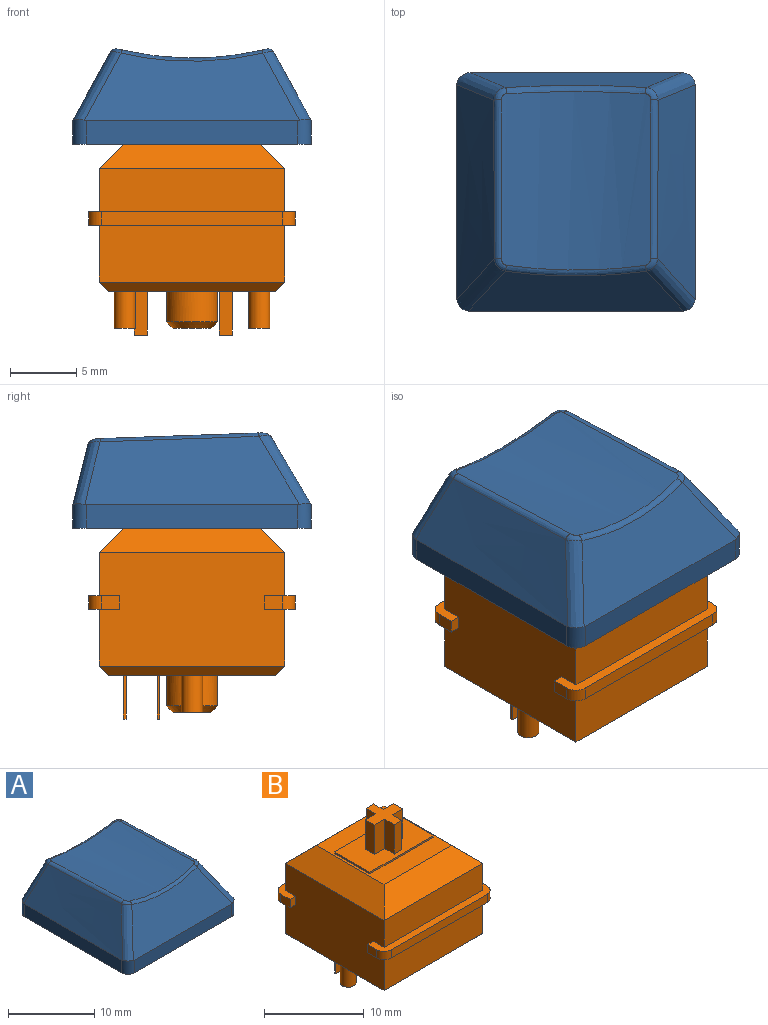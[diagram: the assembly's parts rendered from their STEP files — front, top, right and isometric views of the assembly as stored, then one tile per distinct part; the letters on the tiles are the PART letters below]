
ASSEMBLY  parts=2 mates=1
PART A: 50 faces, bbox 21.6x21x10.3 mm
  f0: plane 18x18mm, normal (0,0,-1), area 67.1mm2, adj f1,f2,f3,f4,f10,f12,f14,f16
  f1: plane 16x1.8mm, normal (1,0,0), area 28.8mm2, adj f0,f8,f10,f16
  f2: plane 16x1.8mm, normal (0,1,0), area 28.8mm2, adj f0,f5,f14,f15,f16,f17
  f3: plane 16x1.8mm, normal (-1,0,0), area 28.8mm2, adj f0,f6,f12,f14
  f4: plane 16x1.8mm, normal (0,-1,0), area 28.8mm2, adj f0,f7,f10,f12
  f5: plane 15.96x4.48mm, normal (0,0.97,0.24), area 56.8mm2, adj f2,f15,f17,f20
  f6: bspline ~18x5.51mm, area 80.2mm2, adj f3,f12,f13,f14,f15,f19
  f7: plane 16.27x5.09mm, normal (0,-0.86,0.51), area 74.6mm2, adj f4,f10,f11,f12,f13,f23
  f8: bspline ~18x5.51mm, area 80.2mm2, adj f1,f10,f11,f16,f17,f24
  f9: cylinder r=22.9mm len=13.32mm, axis (0,1,-0.04), area 149.5mm2, adj f18,f19,f20,f21,f22,f23,f24,f25
  f10: cylinder r=1mm len=1.89mm, axis (0,0,-1), area 2.9mm2, adj f0,f1,f4,f7,f8,f11
  f11: bspline ~6.77x4.7mm, area 8.7mm2, adj f7,f8,f10,f25
  f12: cylinder r=1mm len=1.89mm, axis (0,0,1), area 2.9mm2, adj f0,f3,f4,f6,f7,f13
  f13: bspline ~6.77x4.7mm, area 8.7mm2, adj f6,f7,f12,f21
  f14: cylinder r=1mm len=1.81mm, axis (0,0,-1), area 2.8mm2, adj f0,f2,f3,f6,f15
  f15: bspline ~8.13x5.44mm, area 7.9mm2, adj f2,f5,f6,f14,f18
  f16: cylinder r=1mm len=1.81mm, axis (0,0,1), area 2.8mm2, adj f0,f1,f2,f8,f17
  f17: bspline ~8.13x5.44mm, area 7.9mm2, adj f2,f5,f8,f16,f22
  f18: bspline ~1.19x1.01mm, area 0.7mm2, adj f9,f15,f19,f20
  f19: bspline ~16.72x0.91mm, area 7.8mm2, adj f6,f9,f18,f21
  f20: bspline ~10.66x0.99mm, area 6.9mm2, adj f5,f9,f18,f22
  f21: bspline ~1.2x1.09mm, area 0.6mm2, adj f9,f13,f19,f23
  f22: bspline ~1.17x1.02mm, area 0.7mm2, adj f9,f17,f20,f24
  f23: bspline ~10.72x0.84mm, area 5.8mm2, adj f7,f9,f21,f25
  f24: bspline ~16.72x0.91mm, area 7.8mm2, adj f8,f9,f22,f25
  f25: bspline ~1.2x1.09mm, area 0.6mm2, adj f9,f11,f23,f24
  f26: plane 16.02x1.56mm, normal (-1,0,0), area 24.6mm2, adj f0,f27,f29,f33
  f27: plane 16x1.68mm, normal (0,-1,0), area 26.8mm2, adj f0,f26,f28,f30,f31,f33
  f28: plane 16.02x1.56mm, normal (1,0,0), area 24.6mm2, adj f0,f27,f29,f31
  f29: plane 16.02x1.54mm, normal (0,1,0), area 24.4mm2, adj f0,f26,f28,f32
  f30: plane 16.19x4.4mm, normal (0,-0.97,-0.24), area 50.7mm2, adj f27,f31,f33,f34
  f31: offset ~20x7.51mm, area 71.4mm2, adj f27,f28,f30,f32,f34
  f32: plane 16.71x5.3mm, normal (0,0.86,-0.51), area 66.9mm2, adj f29,f31,f33,f34
  f33: offset ~20x7.51mm, area 71.4mm2, adj f26,f27,f30,f32,f34
  f34: cylinder r=23.9mm len=12.29mm, axis (0,1,-0.04), area 112.6mm2, adj f30,f31,f32,f33,f46
  f35: plane 4.69x1.5mm, normal (-1,0,0), area 7mm2, adj f36,f44,f45,f49
  f36: plane 4.78x1.5mm, normal (0,-1,0), area 7.1mm2, adj f35,f37,f45,f49
  f37: plane 4.82x1.3mm, normal (-1,0,0), area 6.2mm2, adj f36,f38,f45,f49
  f38: plane 4.82x1.5mm, normal (0,1,0), area 7.2mm2, adj f37,f39,f45,f49
  f39: plane 4.79x1.5mm, normal (-1,0,0), area 7.1mm2, adj f38,f40,f45,f49
  f40: plane 4.79x1.3mm, normal (0,1,0), area 6.2mm2, adj f39,f41,f45,f49
  f41: plane 4.79x1.5mm, normal (1,0,0), area 7.1mm2, adj f40,f42,f45,f49
  f42: plane 4.82x1.5mm, normal (0,1,0), area 7.2mm2, adj f41,f43,f45,f49
  f43: plane 4.82x1.3mm, normal (1,0,0), area 6.2mm2, adj f42,f45,f47,f49
  f44: plane 4.64x1.3mm, normal (0,-1,0), area 6mm2, adj f35,f45,f48,f49
  f45: plane 5.5x5.5mm, normal (0,0,-1), area 14.3mm2, adj f35,f36,f37,f38,f39,f40,f41,f42
  f46: cylinder r=2.75mm len=5.5mm, axis (0,0,-1), area 84mm2, adj f34,f45
  f47: plane 4.78x1.5mm, normal (0,-1,0), area 7.1mm2, adj f43,f45,f48,f49
  f48: plane 4.69x1.5mm, normal (1,0,0), area 7mm2, adj f44,f45,f47,f49
  f49: cylinder r=23.9mm len=4.3mm, axis (0,1,-0.04), area 9.5mm2, adj f35,f36,f37,f38,f39,f40,f41,f42
PART B: 69 faces, bbox 15.6x15.6x18.6 mm
  f0: plane 15.6x2.3mm, normal (0,0,-1), area 14.4mm2, adj f2,f3,f28,f30,f35,f60,f62,f63
  f1: plane 15.6x2.3mm, normal (0,0,-1), area 14.4mm2, adj f28,f30,f33,f34,f36,f59,f61,f64
  f2: plane 1.3x1mm, normal (1,0,0), area 1.3mm2, adj f0,f32,f62,f66
  f3: plane 1.3x1mm, normal (-1,0,0), area 1.3mm2, adj f0,f32,f63,f68
  f4: plane 15.6x2.3mm, normal (0,0,1), area 14.4mm2, adj f28,f30,f31,f33,f34,f36,f61,f64
  f5: plane 14x2.2mm, normal (-0.71,0,0.71), area 36.7mm2, adj f6,f7,f26,f30
  f6: plane 14x2.2mm, normal (0,-0.71,0.71), area 36.7mm2, adj f5,f7,f27,f31
  f7: plane 9.6x9.6mm, normal (0,0,1), area 47.2mm2, adj f5,f6,f8,f9,f10,f11,f26,f27
  f8: plane 5x0.2mm, normal (1,0,0), area 1mm2, adj f7,f9,f11,f12
  f9: plane 9x0.2mm, normal (0,1,0), area 1.8mm2, adj f7,f8,f10,f12
  f10: plane 5x0.2mm, normal (-1,0,0), area 1mm2, adj f7,f9,f11,f12
  f11: plane 9x0.2mm, normal (0,-1,0), area 1.8mm2, adj f7,f8,f10,f12
  f12: plane 9x5mm, normal (0,0,1), area 36.9mm2, adj f8,f9,f10,f11,f13,f14,f15,f16
  f13: plane 3.6x1.35mm, normal (1,0,0), area 4.9mm2, adj f12,f14,f24,f25
  f14: plane 3.6x1.08mm, normal (0,1,0), area 3.9mm2, adj f12,f13,f15,f25
  f15: plane 3.6x1.35mm, normal (-1,0,0), area 4.9mm2, adj f12,f14,f16,f25
  f16: plane 3.6x1.46mm, normal (0,1,0), area 5.3mm2, adj f12,f15,f17,f25
  f17: plane 3.6x1.3mm, normal (-1,0,0), area 4.7mm2, adj f12,f16,f18,f25
  f18: plane 3.6x1.46mm, normal (0,-1,0), area 5.3mm2, adj f12,f17,f19,f25
  f19: plane 3.6x1.35mm, normal (-1,0,0), area 4.9mm2, adj f12,f18,f20,f25
  f20: plane 3.6x1.08mm, normal (0,-1,0), area 3.9mm2, adj f12,f19,f21,f25
  f21: plane 3.6x1.35mm, normal (1,0,0), area 4.9mm2, adj f12,f20,f22,f25
  f22: plane 3.6x1.46mm, normal (0,-1,0), area 5.3mm2, adj f12,f21,f23,f25
  f23: plane 3.6x1.3mm, normal (1,0,0), area 4.7mm2, adj f12,f22,f24,f25
  f24: plane 3.6x1.46mm, normal (0,1,0), area 5.3mm2, adj f12,f13,f23,f25
  f25: plane 4x4mm, normal (0,0,1), area 8.1mm2, adj f13,f14,f15,f16,f17,f18,f19,f20
  f26: plane 14x2.2mm, normal (0,0.71,0.71), area 36.7mm2, adj f5,f7,f27,f29
  f27: plane 14x2.2mm, normal (0.71,0,0.71), area 36.7mm2, adj f6,f7,f26,f28
  f28: plane 14x8.6mm, normal (1,0,0), area 117.4mm2, adj f0,f1,f4,f27,f29,f31,f32,f55
  f29: plane 14x3.3mm, normal (0,1,0), area 46.2mm2, adj f26,f28,f30,f32
  f30: plane 14x8.6mm, normal (-1,0,0), area 117.4mm2, adj f0,f1,f4,f5,f29,f31,f32,f57
  f31: plane 14x3.3mm, normal (0,-1,0), area 46.2mm2, adj f4,f6,f28,f30
  f32: plane 15.6x2.3mm, normal (0,0,1), area 14.4mm2, adj f2,f3,f28,f29,f30,f35,f62,f63
  f33: plane 13.6x1mm, normal (0,-1,0), area 13.6mm2, adj f1,f4,f61,f64
  f34: plane 1.3x1mm, normal (1,0,0), area 1.3mm2, adj f1,f4,f61,f65
  f35: plane 13.6x1mm, normal (0,1,0), area 13.6mm2, adj f0,f32,f62,f63
  f36: plane 1.3x1mm, normal (-1,0,0), area 1.3mm2, adj f1,f4,f64,f67
  f37: plane 2.85x2.85mm, normal (0,0,-1), area 6.4mm2, adj f38
  f38: cone r=1.43mm half-angle=45deg, axis (0,0,1), area 7.4mm2, adj f37,f43
  f39: plane 1x0.2mm, normal (0,0,-1), area 0.2mm2, adj f44,f45,f46,f47
  f40: plane 1x0.2mm, normal (0,0,-1), area 0.2mm2, adj f48,f49,f50,f51
  f41: plane 1.6x1.6mm, normal (0,0,-1), area 2mm2, adj f52
  f42: plane 1.6x1.6mm, normal (0,0,-1), area 2mm2, adj f53
  f43: cylinder r=1.93mm len=3.85mm, axis (0,0,1), area 27.8mm2, adj f38,f54
  f44: plane 3.3x0.2mm, normal (-1,0,0), area 0.7mm2, adj f39,f45,f47,f54
  f45: plane 3.3x1mm, normal (0,1,0), area 3.3mm2, adj f39,f44,f46,f54
  f46: plane 3.3x0.2mm, normal (1,0,0), area 0.7mm2, adj f39,f45,f47,f54
  f47: plane 3.3x1mm, normal (0,-1,0), area 3.3mm2, adj f39,f44,f46,f54
  f48: plane 3.3x0.2mm, normal (-1,0,0), area 0.7mm2, adj f40,f49,f51,f54
  f49: plane 3.3x1mm, normal (0,1,0), area 3.3mm2, adj f40,f48,f50,f54
  f50: plane 3.3x0.2mm, normal (1,0,0), area 0.7mm2, adj f40,f49,f51,f54
  f51: plane 3.3x1mm, normal (0,-1,0), area 3.3mm2, adj f40,f48,f50,f54
  f52: cylinder r=0.8mm len=2.8mm, axis (0,0,1), area 14.1mm2, adj f41,f54
  f53: cylinder r=0.8mm len=2.8mm, axis (0,0,1), area 14.1mm2, adj f42,f54
  f54: plane 12.6x12.6mm, normal (0,0,-1), area 142.7mm2, adj f43,f44,f45,f46,f47,f48,f49,f50
  f55: plane 14x0.7mm, normal (0.71,0,-0.71), area 13.2mm2, adj f28,f54,f56,f58
  f56: plane 14x0.7mm, normal (0,0.71,-0.71), area 13.2mm2, adj f54,f55,f57,f60
  f57: plane 14x0.7mm, normal (-0.71,0,-0.71), area 13.2mm2, adj f30,f54,f56,f58
  f58: plane 14x0.7mm, normal (0,-0.71,-0.71), area 13.2mm2, adj f54,f55,f57,f59
  f59: plane 14x4.3mm, normal (0,-1,0), area 60.2mm2, adj f1,f28,f30,f58
  f60: plane 14x4.3mm, normal (0,1,0), area 60.2mm2, adj f0,f28,f30,f56
  f61: cylinder r=1mm len=1mm, axis (0,0,-1), area 1.6mm2, adj f1,f4,f33,f34
  f62: cylinder r=1mm len=1mm, axis (0,0,1), area 1.6mm2, adj f0,f2,f32,f35
  f63: cylinder r=1mm len=1mm, axis (0,0,-1), area 1.6mm2, adj f0,f3,f32,f35
  f64: cylinder r=1mm len=1mm, axis (0,0,1), area 1.6mm2, adj f1,f4,f33,f36
  f65: plane 1x0.8mm, normal (0,1,0), area 0.8mm2, adj f1,f4,f28,f34
  f66: plane 1x0.8mm, normal (0,-1,0), area 0.8mm2, adj f0,f2,f28,f32
  f67: plane 1x0.8mm, normal (0,1,0), area 0.8mm2, adj f1,f4,f30,f36
  f68: plane 1x0.8mm, normal (0,-1,0), area 0.8mm2, adj f0,f3,f30,f32
PLACE A t=(0,0,11.1)mm
PLACE B at identity fixed
MATE fastened B.f38 <-> A.f46  axis (0,0,1) through (0,0,11.7)mm
